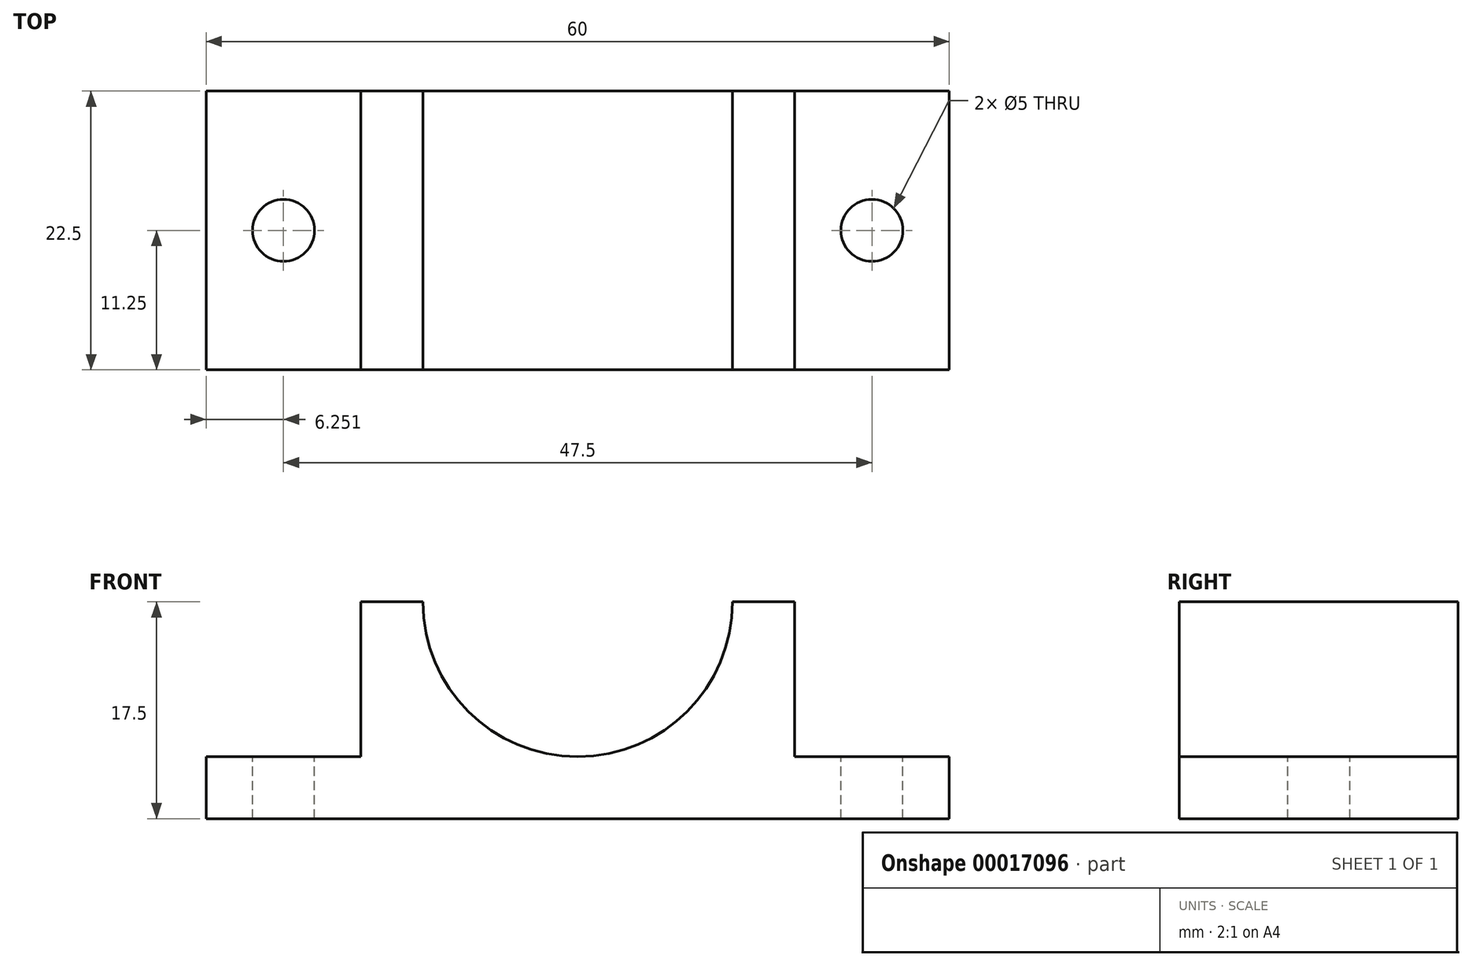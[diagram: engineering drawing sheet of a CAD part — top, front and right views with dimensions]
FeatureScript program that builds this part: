
annotation { "Feature Type Name" : "Feature", "Feature Type Description" : "" }
export const myFeature = defineFeature(function(context is Context, id is Id, definition is map)
    precondition{}
    {
        {
            var Q0;
            Q0=qCreatedBy(makeId("Front.planeOp"),FACE);
            var sketch = newSketch(context, id + "F0", { "sketchPlane" : qUnion([Q0])});
            skLineSegment(sketch, "E0", {"start": v(-40, -25.1) * mm, "end": v(20, -25.1) * mm});
            skLineSegment(sketch, "E1", {"start": v(20, -25.1) * mm, "end": v(20, -20.1) * mm});
            skLineSegment(sketch, "E2", {"start": v(-40, -25.1) * mm, "end": v(-40, -20.1) * mm});
            skLineSegment(sketch, "E3", {"start": v(-40, -20.1) * mm, "end": v(-27.5, -20.1) * mm});
            skLineSegment(sketch, "E4", {"start": v(-27.5, -20.1) * mm, "end": v(-27.5, -7.6) * mm});
            skLineSegment(sketch, "E5", {"start": v(-27.5, -7.6) * mm, "end": v(-22.5, -7.6) * mm});
            skLineSegment(sketch, "E6", {"start": v(20, -20.1) * mm, "end": v(7.5, -20.1) * mm});
            skLineSegment(sketch, "E7", {"start": v(7.5, -20.1) * mm, "end": v(7.5, -7.6) * mm});
            skLineSegment(sketch, "E8", {"start": v(7.5, -7.6) * mm, "end": v(2.5, -7.6) * mm});
            skArc(sketch, "E9", {"start": v(-22.5, -7.6) * mm, "mid": v(-10, -20.1) * mm, "end": v(2.5, -7.6) * mm});
            skSolve(sketch);
        }
        {
            var Q0;
            Q0=makeQuery(id+"F0.imprint","IMPRINT",FACE,{"disambiguationData":[TD([[makeQuery(id+"F0.imprint","IMPRINT",EDGE,{"derivedFrom":sQuery(id+"F0.wireOp",EDGE,"E0")}),1.0]])]});
            extrude(context, id + "F1", {"entities" : qUnion([Q0]), "depth" : 22.5 * mm});
        }
        {
            var Q0;
            Q0=makeQuery(id+"F1.opExtrude","SWEPT_FACE",FACE,{"disambiguationData":[OSD([sQuery(id+"F0.wireOp",EDGE,"E6")])]});
            var sketch = newSketch(context, id + "F2", { "sketchPlane" : qUnion([Q0])});
            skCircle(sketch, "E10", {"center": v(13.75, -11.25) * mm, "radius": 2.5 * mm});
            skSolve(sketch);
        }
        {
            var Q0;
            Q0=makeQuery(id+"F2.imprint","IMPRINT",FACE,{"disambiguationData":[TD([[makeQuery(id+"F2.imprint","IMPRINT",EDGE,{"derivedFrom":sQuery(id+"F2.wireOp",EDGE,"E10")}),1.0]])]});
            extrude(context, id + "F3", {"entities" : qUnion([Q0]), "operationType" : NewBodyOperationType.REMOVE, "endBound" : BoundingType.THROUGH_ALL, "oppositeDirection" : true, "depth" : 25 * mm});
        }
        {
            var Q0;
            Q0=makeQuery(id+"F1.opExtrude","SWEPT_FACE",FACE,{"disambiguationData":[OSD([sQuery(id+"F0.wireOp",EDGE,"E3")])]});
            var sketch = newSketch(context, id + "F4", { "sketchPlane" : qUnion([Q0])});
            skCircle(sketch, "E11", {"center": v(-33.75, -11.25) * mm, "radius": 2.5 * mm});
            skSolve(sketch);
        }
        {
            var Q0;
            Q0=makeQuery(id+"F4.imprint","IMPRINT",FACE,{"disambiguationData":[TD([[makeQuery(id+"F4.imprint","IMPRINT",EDGE,{"derivedFrom":sQuery(id+"F4.wireOp",EDGE,"E11")}),1.0]])]});
            extrude(context, id + "F5", {"entities" : qUnion([Q0]), "operationType" : NewBodyOperationType.REMOVE, "endBound" : BoundingType.THROUGH_ALL, "oppositeDirection" : true, "depth" : 25 * mm});
        }
    });
